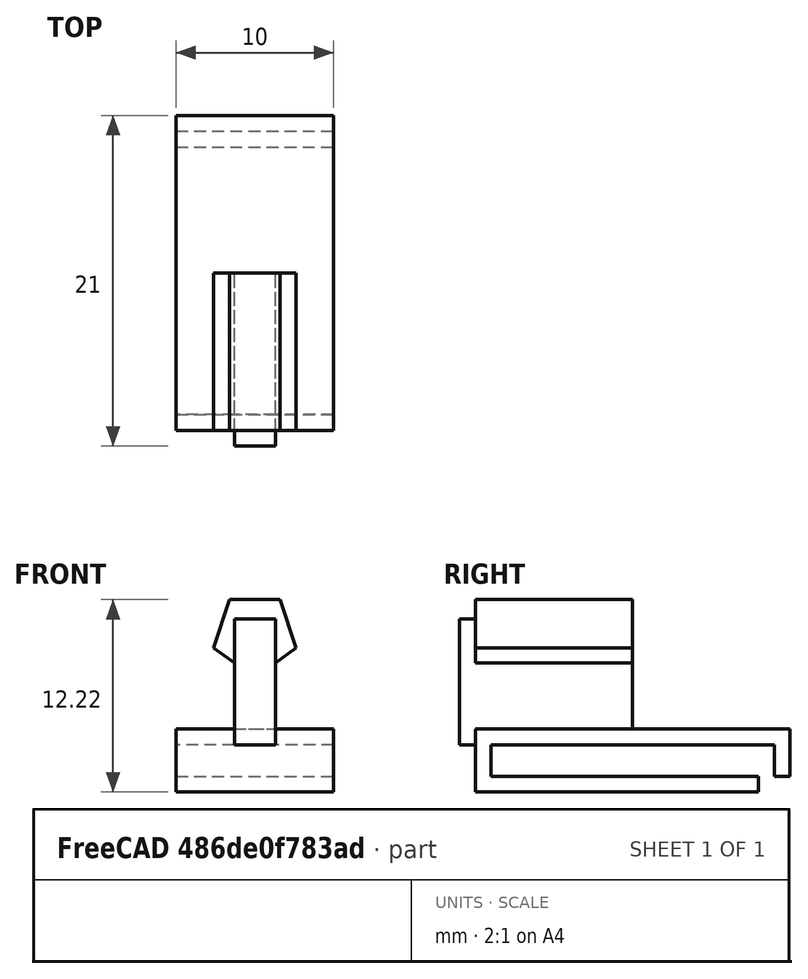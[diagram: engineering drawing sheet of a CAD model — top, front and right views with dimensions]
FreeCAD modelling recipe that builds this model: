
FCSTD DOCUMENT  (FreeCAD 0.18.1R)
Label: flatcablemanagement
License: All rights reserved
LicenseURL: http://en.wikipedia.org/wiki/All_rights_reserved
objects: Part::Box×5, Part::MultiFuse×2, Part::RegularPolygon×1, Part::Extrusion×1
note: 9 computed .brp shape members not serialized (recipe doc carries the construction recipe); baked Part::Feature solids carry a one-line shape summary decoded from their .brp

FEATURE [Part::Box] Box  label="Cube"
  AttacherType = Attacher::AttachEngine3D
  Height = 1
  Length = 10
  Width = 18
FEATURE [Part::Box] Box001  label="Cube001"
  AttacherType = Attacher::AttachEngine3D
  Height = 1
  Length = 10
  Placement = pos=(0,0,3) rot=(0,0,1;0rad)
  Width = 20
FEATURE [Part::Box] Box002  label="Cube002"
  AttacherType = Attacher::AttachEngine3D
  Height = 2
  Length = 10
  Placement = pos=(0,19,1) rot=(0,0,1;0rad)
  Width = 1
FEATURE [Part::Box] Box003  label="Cube003"
  AttacherType = Attacher::AttachEngine3D
  Height = 4
  Length = 10
  Width = 1
FEATURE [Part::RegularPolygon] RegularPolygon003  label="Regular polygon003"
  AttacherType = Attacher::AttachEngine3D
  Circumradius = 2.75
  Placement = pos=(-3,7,0) rot=(0,0,1;0rad)
  Polygon = 5
FEATURE [Part::Extrusion] Extrude003
  Base = -> RegularPolygon003
  Dir = (0,0,1)
  DirMode = 2
  FaceMakerClass = Part::FaceMakerBullseye
  LengthFwd = 10
  LengthRev = 0
  Placement = pos=(0,0,0) rot=(0,1,0;1.5708rad)
  Solid = true
  Symmetric = false
FEATURE [Part::Box] Box004  label="Cube004"
  AttacherType = Attacher::AttachEngine3D
  Height = 8
  Length = 11
  Placement = pos=(0,5.7,-4) rot=(0,0,1;0rad)
  Width = 2.6
FEATURE [Part::MultiFuse] Fusion003  label="keymaster"
  Placement = pos=(-2,10,7) rot=(0,0,1;4.71239rad)
  Shapes = -> [Extrude003,Box004]
FEATURE [Part::MultiFuse] Fusion
  Shapes = -> [Box002,Box001,Fusion003,Box003,Box]
